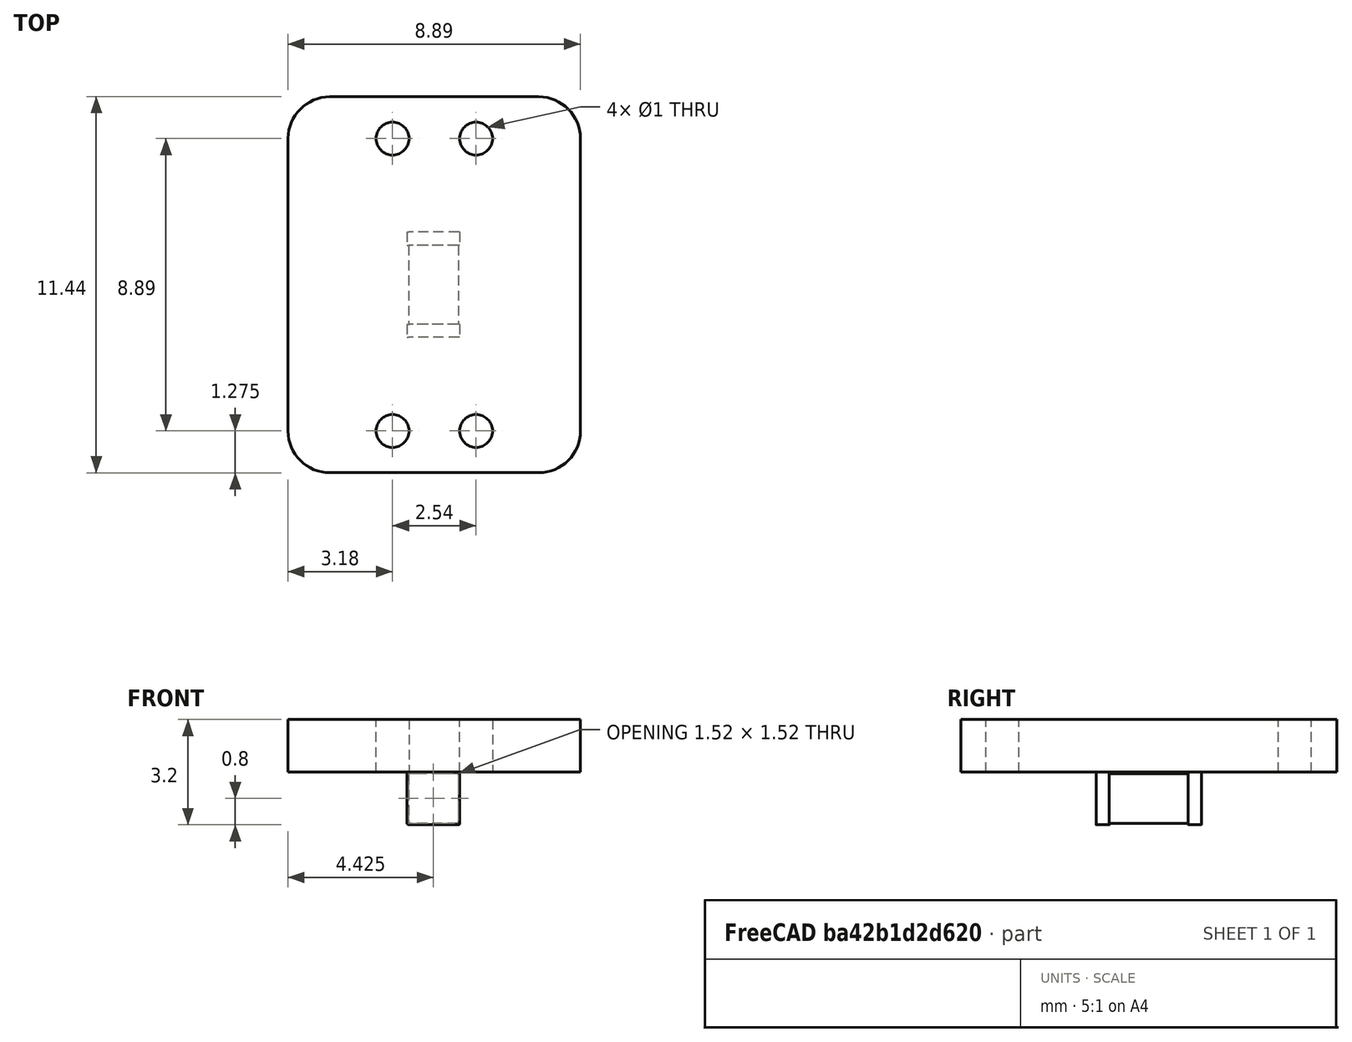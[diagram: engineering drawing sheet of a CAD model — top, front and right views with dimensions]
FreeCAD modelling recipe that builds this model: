
FCSTD DOCUMENT  (FreeCAD 0.16R6712 (Git))
Label: ws2812b_reverse
License: All rights reserved
LicenseURL: http://en.wikipedia.org/wiki/All_rights_reserved
objects: Part::Feature×2, App::DocumentObjectGroup×2, Sketcher::SketchObject×1
note: 3 computed .brp shape members not serialized (recipe doc carries the construction recipe); baked Part::Feature solids carry a one-line shape summary decoded from their .brp

FEATURE [Part::Feature] Pcb
  Placement = pos=(-144.145,107.315,0) rot=(0,0,1;0rad)
  shape: bbox 8.91 x 11.45 x 1.62 mm, 14 faces (baked)
FEATURE [Sketcher::SketchObject] PCB_Sketch
  sketch-geometry (8):
    g0: LineSegment StartX=4.445 StartY=-4.445 StartZ=0 EndX=4.445 EndY=4.445 EndZ=0
    g1: LineSegment StartX=-3.175 StartY=-5.715 StartZ=0 EndX=3.175 EndY=-5.715 EndZ=0
    g2: LineSegment StartX=-4.445 StartY=4.445 StartZ=0 EndX=-4.445 EndY=-4.445 EndZ=0
    g3: LineSegment StartX=3.175 StartY=5.715 StartZ=0 EndX=-3.175 EndY=5.715 EndZ=0
    g4: ArcOfCircle CenterX=3.175 CenterY=-4.445 CenterZ=0 NormalX=0 NormalY=0 NormalZ=1 Radius=1.27 StartAngle=4.71239 EndAngle=6.28319
    g5: ArcOfCircle CenterX=-3.175 CenterY=-4.445 CenterZ=0 NormalX=0 NormalY=0 NormalZ=1 Radius=1.27 StartAngle=3.14159 EndAngle=4.71239
    g6: ArcOfCircle CenterX=-3.175 CenterY=4.445 CenterZ=0 NormalX=0 NormalY=0 NormalZ=1 Radius=1.27 StartAngle=1.5708 EndAngle=3.14159
    g7: ArcOfCircle CenterX=3.175 CenterY=4.445 CenterZ=0 NormalX=0 NormalY=0 NormalZ=1 Radius=1.27 StartAngle=0 EndAngle=1.5708
FEATURE [App::DocumentObjectGroup] Board_Geoms
  Group = -> [Pcb,PCB_Sketch]
FEATURE [Part::Feature] Shape  label="C_1206_3216Metric_"
  Placement = pos=(-0.0254,0,-1.6) rot=(-0.707107,0.707107,0;3.14159rad)
  shape: bbox 1.6 x 3.2 x 1.6 mm, 28 faces (baked)
FEATURE [App::DocumentObjectGroup] Step_Models
  Group = -> [Shape]
